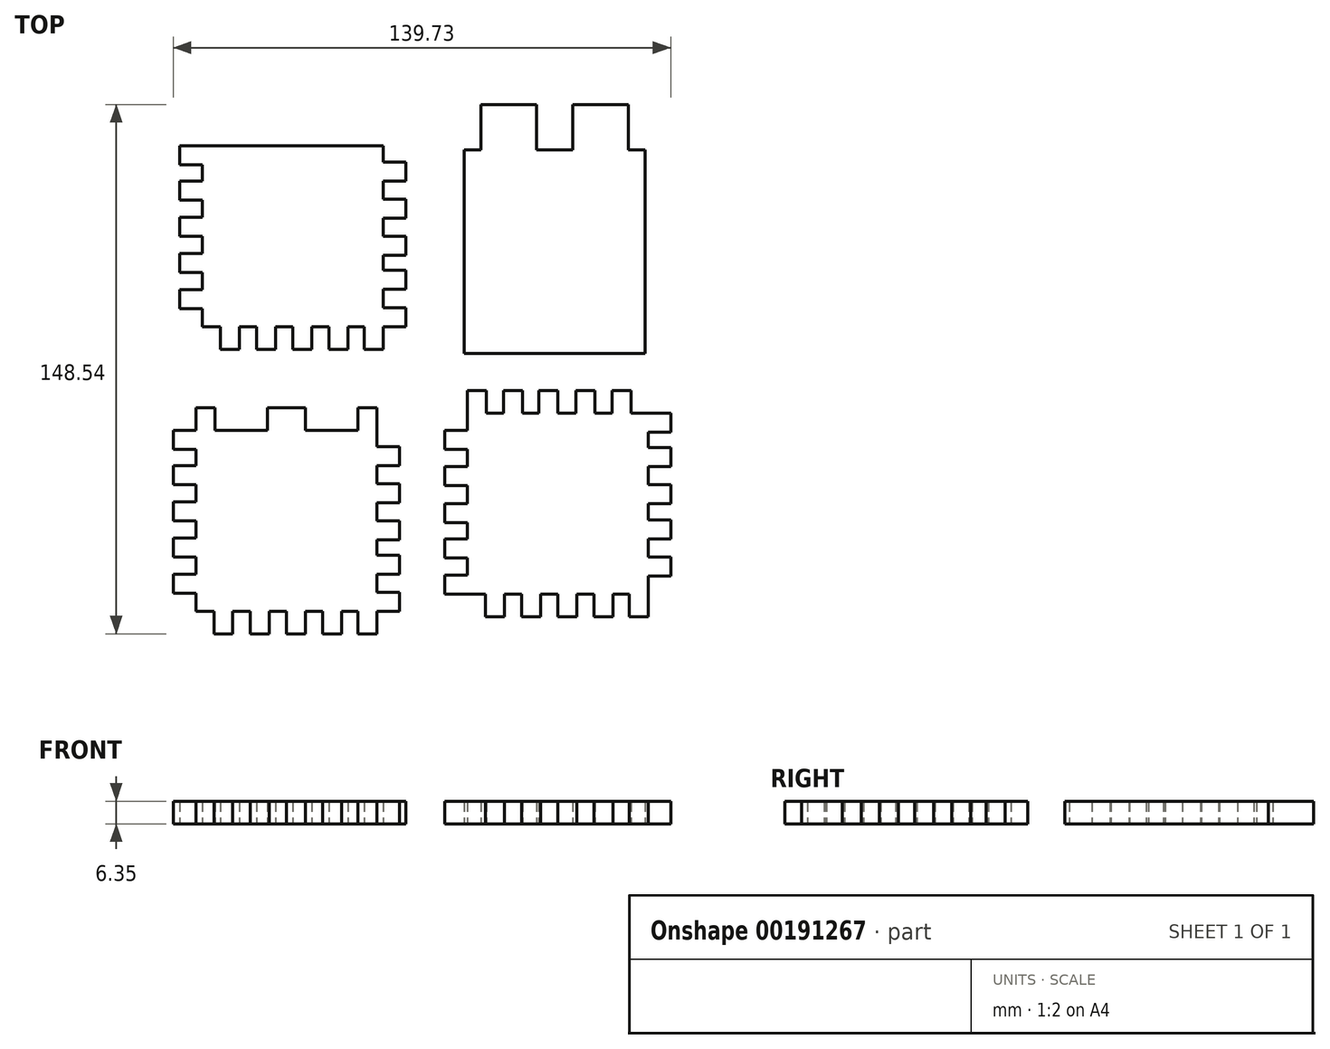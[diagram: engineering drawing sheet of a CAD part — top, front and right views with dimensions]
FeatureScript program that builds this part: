
annotation { "Feature Type Name" : "Feature", "Feature Type Description" : "" }
export const myFeature = defineFeature(function(context is Context, id is Id, definition is map)
    precondition{}
    {
        {
            var Q0;
            Q0=qCreatedBy(makeId("Top.planeOp"),FACE);
            var sketch = newSketch(context, id + "F0", { "sketchPlane" : qUnion([Q0])});
            skLineSegment(sketch, "E0.bottom", {"start": v(-10.8, 18.02) * mm, "end": v(-61.6, 18.02) * mm});
            skLineSegment(sketch, "E0.top", {"start": v(-10.8, 68.82) * mm, "end": v(-61.6, 68.82) * mm});
            skLineSegment(sketch, "E0.left", {"start": v(-10.8, 18.02) * mm, "end": v(-10.8, 68.82) * mm});
            skLineSegment(sketch, "E0.right", {"start": v(-61.6, 18.02) * mm, "end": v(-61.6, 68.82) * mm});
            skLineSegment(sketch, "E1.bottom", {"start": v(-61.6, 68.82) * mm, "end": v(-67.96, 68.82) * mm});
            skLineSegment(sketch, "E1.top", {"start": v(-61.6, 63.48) * mm, "end": v(-67.96, 63.48) * mm});
            skLineSegment(sketch, "E1.left", {"start": v(-61.6, 68.82) * mm, "end": v(-61.6, 63.48) * mm});
            skLineSegment(sketch, "E1.right", {"start": v(-67.96, 68.82) * mm, "end": v(-67.96, 63.48) * mm});
            skLineSegment(sketch, "E2.top", {"start": v(-61.6, 58.91) * mm, "end": v(-67.96, 58.91) * mm});
            skLineSegment(sketch, "E2.left", {"start": v(-61.6, 63.48) * mm, "end": v(-61.6, 58.91) * mm});
            skLineSegment(sketch, "E3.top", {"start": v(-61.6, 53.58) * mm, "end": v(-67.96, 53.58) * mm});
            skLineSegment(sketch, "E3.left", {"start": v(-61.6, 58.91) * mm, "end": v(-61.6, 53.58) * mm});
            skLineSegment(sketch, "E3.right", {"start": v(-67.96, 58.91) * mm, "end": v(-67.96, 53.58) * mm});
            skLineSegment(sketch, "E4.left", {"start": v(-61.6, 53.58) * mm, "end": v(-61.6, 48.75) * mm});
            skLineSegment(sketch, "E5.bottom", {"start": v(-61.6, 48.75) * mm, "end": v(-67.96, 48.75) * mm});
            skLineSegment(sketch, "E5.left", {"start": v(-61.6, 48.75) * mm, "end": v(-61.6, 53.58) * mm});
            skLineSegment(sketch, "E6.left", {"start": v(-61.6, 48.75) * mm, "end": v(-61.6, 38.6) * mm});
            skLineSegment(sketch, "E7.bottom", {"start": v(-67.96, 48.75) * mm, "end": v(-61.6, 48.75) * mm});
            skLineSegment(sketch, "E7.top", {"start": v(-67.96, 43.42) * mm, "end": v(-61.6, 43.42) * mm});
            skLineSegment(sketch, "E7.left", {"start": v(-67.96, 48.75) * mm, "end": v(-67.96, 43.42) * mm});
            skLineSegment(sketch, "E7.right", {"start": v(-61.6, 48.75) * mm, "end": v(-61.6, 43.42) * mm});
            skLineSegment(sketch, "E8.top", {"start": v(-67.96, 38.6) * mm, "end": v(-61.6, 38.6) * mm});
            skLineSegment(sketch, "E8.right", {"start": v(-61.6, 43.42) * mm, "end": v(-61.6, 38.6) * mm});
            skLineSegment(sketch, "E9.top", {"start": v(-67.96, 33.26) * mm, "end": v(-61.6, 33.26) * mm});
            skLineSegment(sketch, "E9.left", {"start": v(-67.96, 38.6) * mm, "end": v(-67.96, 33.26) * mm});
            skLineSegment(sketch, "E9.right", {"start": v(-61.6, 38.6) * mm, "end": v(-61.6, 33.26) * mm});
            skLineSegment(sketch, "E10.top", {"start": v(-67.96, 28.43) * mm, "end": v(-61.6, 28.43) * mm});
            skLineSegment(sketch, "E10.right", {"start": v(-61.6, 33.26) * mm, "end": v(-61.6, 28.43) * mm});
            skLineSegment(sketch, "E11.top", {"start": v(-67.96, 23.1) * mm, "end": v(-61.6, 23.1) * mm});
            skLineSegment(sketch, "E11.left", {"start": v(-67.96, 28.43) * mm, "end": v(-67.96, 23.1) * mm});
            skLineSegment(sketch, "E11.right", {"start": v(-61.6, 28.43) * mm, "end": v(-61.6, 23.1) * mm});
            skLineSegment(sketch, "E12.right", {"start": v(-61.6, 23.1) * mm, "end": v(-61.6, 18.02) * mm});
            skLineSegment(sketch, "E13.top", {"start": v(-10.8, 64.24) * mm, "end": v(-4.46, 64.24) * mm});
            skLineSegment(sketch, "E13.left", {"start": v(-10.8, 68.82) * mm, "end": v(-10.8, 64.24) * mm});
            skLineSegment(sketch, "E14.bottom", {"start": v(-4.46, 64.24) * mm, "end": v(-10.8, 64.24) * mm});
            skLineSegment(sketch, "E14.top", {"start": v(-4.46, 58.91) * mm, "end": v(-10.8, 58.91) * mm});
            skLineSegment(sketch, "E14.left", {"start": v(-4.46, 64.24) * mm, "end": v(-4.46, 58.91) * mm});
            skLineSegment(sketch, "E14.right", {"start": v(-10.8, 64.24) * mm, "end": v(-10.8, 58.91) * mm});
            skLineSegment(sketch, "E15.top", {"start": v(-4.46, 53.83) * mm, "end": v(-10.8, 53.83) * mm});
            skLineSegment(sketch, "E15.right", {"start": v(-10.8, 58.91) * mm, "end": v(-10.8, 53.83) * mm});
            skLineSegment(sketch, "E16.top", {"start": v(-4.46, 48.5) * mm, "end": v(-10.8, 48.5) * mm});
            skLineSegment(sketch, "E16.left", {"start": v(-4.46, 53.83) * mm, "end": v(-4.46, 48.5) * mm});
            skLineSegment(sketch, "E16.right", {"start": v(-10.8, 53.83) * mm, "end": v(-10.8, 48.5) * mm});
            skLineSegment(sketch, "E17.top", {"start": v(-4.46, 43.42) * mm, "end": v(-10.8, 43.42) * mm});
            skLineSegment(sketch, "E17.right", {"start": v(-10.8, 48.5) * mm, "end": v(-10.8, 43.42) * mm});
            skLineSegment(sketch, "E18.top", {"start": v(-4.46, 38.08) * mm, "end": v(-10.8, 38.08) * mm});
            skLineSegment(sketch, "E18.left", {"start": v(-4.46, 43.42) * mm, "end": v(-4.46, 38.08) * mm});
            skLineSegment(sketch, "E18.right", {"start": v(-10.8, 43.42) * mm, "end": v(-10.8, 38.08) * mm});
            skLineSegment(sketch, "E19.top", {"start": v(-4.46, 33.9) * mm, "end": v(-10.8, 33.9) * mm});
            skLineSegment(sketch, "E19.right", {"start": v(-10.8, 38.08) * mm, "end": v(-10.8, 33.9) * mm});
            skLineSegment(sketch, "E20.top", {"start": v(-4.46, 28.56) * mm, "end": v(-10.8, 28.56) * mm});
            skLineSegment(sketch, "E20.left", {"start": v(-4.46, 33.9) * mm, "end": v(-4.46, 28.56) * mm});
            skLineSegment(sketch, "E20.right", {"start": v(-10.8, 33.9) * mm, "end": v(-10.8, 28.56) * mm});
            skLineSegment(sketch, "E21.top", {"start": v(-4.46, 23.35) * mm, "end": v(-10.8, 23.35) * mm});
            skLineSegment(sketch, "E21.right", {"start": v(-10.8, 28.56) * mm, "end": v(-10.8, 23.35) * mm});
            skLineSegment(sketch, "E22.top", {"start": v(-4.46, 18.02) * mm, "end": v(-10.8, 18.02) * mm});
            skLineSegment(sketch, "E22.left", {"start": v(-4.46, 23.35) * mm, "end": v(-4.46, 18.02) * mm});
            skLineSegment(sketch, "E22.right", {"start": v(-10.8, 23.35) * mm, "end": v(-10.8, 18.02) * mm});
            skLineSegment(sketch, "E23.bottom", {"start": v(-10.8, 18.02) * mm, "end": v(-16.14, 18.02) * mm});
            skLineSegment(sketch, "E23.top", {"start": v(-10.8, 11.67) * mm, "end": v(-16.14, 11.67) * mm});
            skLineSegment(sketch, "E23.left", {"start": v(-10.8, 18.02) * mm, "end": v(-10.8, 11.67) * mm});
            skLineSegment(sketch, "E23.right", {"start": v(-16.14, 18.02) * mm, "end": v(-16.14, 11.67) * mm});
            skLineSegment(sketch, "E24.top", {"start": v(-16.14, 18.02) * mm, "end": v(-20.71, 18.02) * mm});
            skLineSegment(sketch, "E24.left", {"start": v(-16.14, 11.67) * mm, "end": v(-16.14, 18.02) * mm});
            skLineSegment(sketch, "E24.right", {"start": v(-20.71, 11.67) * mm, "end": v(-20.71, 18.02) * mm});
            skLineSegment(sketch, "E25.bottom", {"start": v(-20.71, 11.67) * mm, "end": v(-26.05, 11.67) * mm});
            skLineSegment(sketch, "E25.top", {"start": v(-20.71, 18.02) * mm, "end": v(-26.05, 18.02) * mm});
            skLineSegment(sketch, "E25.right", {"start": v(-26.05, 11.67) * mm, "end": v(-26.05, 18.02) * mm});
            skLineSegment(sketch, "E26.top", {"start": v(-26.05, 18.02) * mm, "end": v(-30.87, 18.02) * mm});
            skLineSegment(sketch, "E26.right", {"start": v(-30.87, 11.67) * mm, "end": v(-30.87, 18.02) * mm});
            skLineSegment(sketch, "E27.bottom", {"start": v(-30.87, 11.67) * mm, "end": v(-36.2, 11.67) * mm});
            skLineSegment(sketch, "E27.top", {"start": v(-30.87, 18.02) * mm, "end": v(-36.2, 18.02) * mm});
            skLineSegment(sketch, "E27.right", {"start": v(-36.2, 11.67) * mm, "end": v(-36.2, 18.02) * mm});
            skLineSegment(sketch, "E28.top", {"start": v(-36.2, 18.02) * mm, "end": v(-41.03, 18.02) * mm});
            skLineSegment(sketch, "E28.right", {"start": v(-41.03, 11.67) * mm, "end": v(-41.03, 18.02) * mm});
            skLineSegment(sketch, "E29.bottom", {"start": v(-41.03, 11.67) * mm, "end": v(-46.37, 11.67) * mm});
            skLineSegment(sketch, "E29.top", {"start": v(-41.03, 18.02) * mm, "end": v(-46.37, 18.02) * mm});
            skLineSegment(sketch, "E29.right", {"start": v(-46.37, 11.67) * mm, "end": v(-46.37, 18.02) * mm});
            skLineSegment(sketch, "E30.top", {"start": v(-46.37, 18.02) * mm, "end": v(-51.2, 18.02) * mm});
            skLineSegment(sketch, "E30.right", {"start": v(-51.2, 11.67) * mm, "end": v(-51.2, 18.02) * mm});
            skLineSegment(sketch, "E31.bottom", {"start": v(-51.2, 11.67) * mm, "end": v(-56.53, 11.67) * mm});
            skLineSegment(sketch, "E31.top", {"start": v(-51.2, 18.02) * mm, "end": v(-56.53, 18.02) * mm});
            skLineSegment(sketch, "E31.right", {"start": v(-56.53, 11.67) * mm, "end": v(-56.53, 18.02) * mm});
            skLineSegment(sketch, "E32.top", {"start": v(-56.53, 18.02) * mm, "end": v(-61.6, 18.02) * mm});
            skSolve(sketch);
        }
        {
            var Q0;
            Q0 = qSketchRegion(id + "F0", true);
            extrude(context, id + "F1", {"entities" : qUnion([Q0]), "depth" : 6.35 * mm});
        }
        {
            var Q0;
            Q0=qCreatedBy(makeId("Top.planeOp"),FACE);
            var sketch = newSketch(context, id + "F2", { "sketchPlane" : qUnion([Q0])});
            skLineSegment(sketch, "E33.bottom", {"start": v(12.75, -6.35) * mm, "end": v(63.55, -6.35) * mm});
            skLineSegment(sketch, "E33.top", {"start": v(12.75, -57.15) * mm, "end": v(63.55, -57.15) * mm});
            skLineSegment(sketch, "E33.left", {"start": v(12.75, -6.35) * mm, "end": v(12.75, -57.15) * mm});
            skLineSegment(sketch, "E33.right", {"start": v(63.55, -6.35) * mm, "end": v(63.55, -57.15) * mm});
            skLineSegment(sketch, "E34.bottom", {"start": v(12.75, -6.35) * mm, "end": v(18.09, -6.35) * mm});
            skLineSegment(sketch, "E34.top", {"start": v(12.75, 0) * mm, "end": v(18.09, 0) * mm});
            skLineSegment(sketch, "E34.left", {"start": v(12.75, -6.35) * mm, "end": v(12.75, 0) * mm});
            skLineSegment(sketch, "E34.right", {"start": v(18.09, -6.35) * mm, "end": v(18.09, 0) * mm});
            skLineSegment(sketch, "E35.top", {"start": v(18.09, -6.35) * mm, "end": v(22.91, -6.35) * mm});
            skLineSegment(sketch, "E35.left", {"start": v(18.09, 0) * mm, "end": v(18.09, -6.35) * mm});
            skLineSegment(sketch, "E35.right", {"start": v(22.91, 0) * mm, "end": v(22.91, -6.35) * mm});
            skLineSegment(sketch, "E36.bottom", {"start": v(22.91, 0) * mm, "end": v(28.25, 0) * mm});
            skLineSegment(sketch, "E36.top", {"start": v(22.91, -6.35) * mm, "end": v(28.25, -6.35) * mm});
            skLineSegment(sketch, "E36.right", {"start": v(28.25, 0) * mm, "end": v(28.25, -6.35) * mm});
            skLineSegment(sketch, "E37.top", {"start": v(28.25, -6.35) * mm, "end": v(32.82, -6.35) * mm});
            skLineSegment(sketch, "E37.right", {"start": v(32.82, 0) * mm, "end": v(32.82, -6.35) * mm});
            skLineSegment(sketch, "E38.bottom", {"start": v(32.82, 0) * mm, "end": v(38.15, 0) * mm});
            skLineSegment(sketch, "E38.top", {"start": v(32.82, -6.35) * mm, "end": v(38.15, -6.35) * mm});
            skLineSegment(sketch, "E38.right", {"start": v(38.15, 0) * mm, "end": v(38.15, -6.35) * mm});
            skLineSegment(sketch, "E39.top", {"start": v(38.15, -6.35) * mm, "end": v(43.23, -6.35) * mm});
            skLineSegment(sketch, "E39.right", {"start": v(43.23, 0) * mm, "end": v(43.23, -6.35) * mm});
            skLineSegment(sketch, "E40.bottom", {"start": v(43.23, 0) * mm, "end": v(48.57, 0) * mm});
            skLineSegment(sketch, "E40.top", {"start": v(43.23, -6.35) * mm, "end": v(48.57, -6.35) * mm});
            skLineSegment(sketch, "E40.right", {"start": v(48.57, 0) * mm, "end": v(48.57, -6.35) * mm});
            skLineSegment(sketch, "E41.top", {"start": v(48.57, -6.35) * mm, "end": v(53.4, -6.35) * mm});
            skLineSegment(sketch, "E41.right", {"start": v(53.4, 0) * mm, "end": v(53.4, -6.35) * mm});
            skLineSegment(sketch, "E42.bottom", {"start": v(53.4, -6.35) * mm, "end": v(58.73, -6.35) * mm});
            skLineSegment(sketch, "E42.top", {"start": v(53.4, 0) * mm, "end": v(58.73, 0) * mm});
            skLineSegment(sketch, "E42.left", {"start": v(53.4, -6.35) * mm, "end": v(53.4, 0) * mm});
            skLineSegment(sketch, "E42.right", {"start": v(58.73, -6.35) * mm, "end": v(58.73, 0) * mm});
            skLineSegment(sketch, "E43.bottom", {"start": v(63.55, -6.35) * mm, "end": v(58.73, -6.35) * mm});
            skLineSegment(sketch, "E44.top", {"start": v(12.75, -11.18) * mm, "end": v(6.4, -11.18) * mm});
            skLineSegment(sketch, "E44.left", {"start": v(12.75, -6.35) * mm, "end": v(12.75, -11.18) * mm});
            skLineSegment(sketch, "E45.bottom", {"start": v(6.4, -11.18) * mm, "end": v(12.75, -11.18) * mm});
            skLineSegment(sketch, "E45.top", {"start": v(6.4, -16.5) * mm, "end": v(12.75, -16.5) * mm});
            skLineSegment(sketch, "E45.left", {"start": v(6.4, -11.18) * mm, "end": v(6.4, -16.5) * mm});
            skLineSegment(sketch, "E45.right", {"start": v(12.75, -11.18) * mm, "end": v(12.75, -16.5) * mm});
            skLineSegment(sketch, "E46.top", {"start": v(6.4, -21.34) * mm, "end": v(12.75, -21.34) * mm});
            skLineSegment(sketch, "E46.right", {"start": v(12.75, -16.5) * mm, "end": v(12.75, -21.34) * mm});
            skLineSegment(sketch, "E47.top", {"start": v(6.4, -26.67) * mm, "end": v(12.75, -26.67) * mm});
            skLineSegment(sketch, "E47.left", {"start": v(6.4, -21.34) * mm, "end": v(6.4, -26.67) * mm});
            skLineSegment(sketch, "E47.right", {"start": v(12.75, -21.34) * mm, "end": v(12.75, -26.67) * mm});
            skLineSegment(sketch, "E48.top", {"start": v(6.4, -31.75) * mm, "end": v(12.75, -31.75) * mm});
            skLineSegment(sketch, "E48.right", {"start": v(12.75, -26.67) * mm, "end": v(12.75, -31.75) * mm});
            skLineSegment(sketch, "E49.top", {"start": v(6.4, -37.08) * mm, "end": v(12.75, -37.08) * mm});
            skLineSegment(sketch, "E49.left", {"start": v(6.4, -31.75) * mm, "end": v(6.4, -37.08) * mm});
            skLineSegment(sketch, "E50.top", {"start": v(6.4, -41.66) * mm, "end": v(12.75, -41.66) * mm});
            skLineSegment(sketch, "E50.right", {"start": v(12.75, -37.08) * mm, "end": v(12.75, -41.66) * mm});
            skLineSegment(sketch, "E51.top", {"start": v(6.4, -47) * mm, "end": v(12.75, -47) * mm});
            skLineSegment(sketch, "E51.left", {"start": v(6.4, -41.66) * mm, "end": v(6.4, -47) * mm});
            skLineSegment(sketch, "E51.right", {"start": v(12.75, -41.66) * mm, "end": v(12.75, -47) * mm});
            skLineSegment(sketch, "E52.top", {"start": v(6.4, -51.82) * mm, "end": v(12.75, -51.82) * mm});
            skLineSegment(sketch, "E52.right", {"start": v(12.75, -47) * mm, "end": v(12.75, -51.82) * mm});
            skLineSegment(sketch, "E53.top", {"start": v(6.4, -57.15) * mm, "end": v(12.75, -57.15) * mm});
            skLineSegment(sketch, "E53.left", {"start": v(6.4, -51.82) * mm, "end": v(6.4, -57.15) * mm});
            skLineSegment(sketch, "E53.right", {"start": v(12.75, -51.82) * mm, "end": v(12.75, -57.15) * mm});
            skLineSegment(sketch, "E54.bottom", {"start": v(12.75, -57.15) * mm, "end": v(17.83, -57.15) * mm});
            skLineSegment(sketch, "E54.right", {"start": v(17.83, -57.15) * mm, "end": v(17.83, -63.5) * mm});
            skLineSegment(sketch, "E55.bottom", {"start": v(17.83, -63.5) * mm, "end": v(23.17, -63.5) * mm});
            skLineSegment(sketch, "E55.top", {"start": v(17.83, -57.15) * mm, "end": v(23.17, -57.15) * mm});
            skLineSegment(sketch, "E55.left", {"start": v(17.83, -63.5) * mm, "end": v(17.83, -57.15) * mm});
            skLineSegment(sketch, "E55.right", {"start": v(23.17, -63.5) * mm, "end": v(23.17, -57.15) * mm});
            skLineSegment(sketch, "E56.top", {"start": v(23.17, -57.15) * mm, "end": v(28, -57.15) * mm});
            skLineSegment(sketch, "E56.right", {"start": v(28, -63.5) * mm, "end": v(28, -57.15) * mm});
            skLineSegment(sketch, "E57.bottom", {"start": v(28, -63.5) * mm, "end": v(33.33, -63.5) * mm});
            skLineSegment(sketch, "E57.top", {"start": v(28, -57.15) * mm, "end": v(33.33, -57.15) * mm});
            skLineSegment(sketch, "E57.right", {"start": v(33.33, -63.5) * mm, "end": v(33.33, -57.15) * mm});
            skLineSegment(sketch, "E58.top", {"start": v(33.33, -57.15) * mm, "end": v(38.15, -57.15) * mm});
            skLineSegment(sketch, "E58.right", {"start": v(38.15, -63.5) * mm, "end": v(38.15, -57.15) * mm});
            skLineSegment(sketch, "E59.bottom", {"start": v(38.15, -63.5) * mm, "end": v(43.49, -63.5) * mm});
            skLineSegment(sketch, "E59.top", {"start": v(38.15, -57.15) * mm, "end": v(43.49, -57.15) * mm});
            skLineSegment(sketch, "E59.right", {"start": v(43.49, -63.5) * mm, "end": v(43.49, -57.15) * mm});
            skLineSegment(sketch, "E60.top", {"start": v(43.49, -57.15) * mm, "end": v(48.31, -57.15) * mm});
            skLineSegment(sketch, "E60.right", {"start": v(48.31, -63.5) * mm, "end": v(48.31, -57.15) * mm});
            skLineSegment(sketch, "E61.bottom", {"start": v(48.31, -63.5) * mm, "end": v(53.65, -63.5) * mm});
            skLineSegment(sketch, "E61.top", {"start": v(48.31, -57.15) * mm, "end": v(53.65, -57.15) * mm});
            skLineSegment(sketch, "E61.right", {"start": v(53.65, -63.5) * mm, "end": v(53.65, -57.15) * mm});
            skLineSegment(sketch, "E62.top", {"start": v(53.65, -57.15) * mm, "end": v(58.22, -57.15) * mm});
            skLineSegment(sketch, "E62.right", {"start": v(58.22, -63.5) * mm, "end": v(58.22, -57.15) * mm});
            skLineSegment(sketch, "E63.bottom", {"start": v(58.22, -63.5) * mm, "end": v(63.55, -63.5) * mm});
            skLineSegment(sketch, "E63.top", {"start": v(58.22, -57.15) * mm, "end": v(63.55, -57.15) * mm});
            skLineSegment(sketch, "E63.right", {"start": v(63.55, -63.5) * mm, "end": v(63.55, -57.15) * mm});
            skLineSegment(sketch, "E64.bottom", {"start": v(63.55, -6.35) * mm, "end": v(69.9, -6.35) * mm});
            skLineSegment(sketch, "E64.top", {"start": v(63.55, -11.68) * mm, "end": v(69.9, -11.68) * mm});
            skLineSegment(sketch, "E64.left", {"start": v(63.55, -6.35) * mm, "end": v(63.55, -11.68) * mm});
            skLineSegment(sketch, "E64.right", {"start": v(69.9, -6.35) * mm, "end": v(69.9, -11.68) * mm});
            skLineSegment(sketch, "E65.bottom", {"start": v(69.9, -11.68) * mm, "end": v(63.55, -11.68) * mm});
            skLineSegment(sketch, "E65.top", {"start": v(69.9, -16) * mm, "end": v(63.55, -16) * mm});
            skLineSegment(sketch, "E65.right", {"start": v(63.55, -11.68) * mm, "end": v(63.55, -16) * mm});
            skLineSegment(sketch, "E66.top", {"start": v(69.9, -21.34) * mm, "end": v(63.55, -21.34) * mm});
            skLineSegment(sketch, "E66.left", {"start": v(69.9, -16) * mm, "end": v(69.9, -21.34) * mm});
            skLineSegment(sketch, "E66.right", {"start": v(63.55, -16) * mm, "end": v(63.55, -21.34) * mm});
            skLineSegment(sketch, "E67.top", {"start": v(69.9, -26.42) * mm, "end": v(63.55, -26.42) * mm});
            skLineSegment(sketch, "E67.right", {"start": v(63.55, -21.34) * mm, "end": v(63.55, -26.42) * mm});
            skLineSegment(sketch, "E68.top", {"start": v(69.9, -31.75) * mm, "end": v(63.55, -31.75) * mm});
            skLineSegment(sketch, "E68.left", {"start": v(69.9, -26.42) * mm, "end": v(69.9, -31.75) * mm});
            skLineSegment(sketch, "E68.right", {"start": v(63.55, -26.42) * mm, "end": v(63.55, -31.75) * mm});
            skLineSegment(sketch, "E69.top", {"start": v(69.9, -36.32) * mm, "end": v(63.55, -36.32) * mm});
            skLineSegment(sketch, "E69.right", {"start": v(63.55, -31.75) * mm, "end": v(63.55, -36.32) * mm});
            skLineSegment(sketch, "E70.top", {"start": v(69.9, -41.66) * mm, "end": v(63.55, -41.66) * mm});
            skLineSegment(sketch, "E70.left", {"start": v(69.9, -36.32) * mm, "end": v(69.9, -41.66) * mm});
            skLineSegment(sketch, "E70.right", {"start": v(63.55, -36.32) * mm, "end": v(63.55, -41.66) * mm});
            skLineSegment(sketch, "E71.top", {"start": v(69.9, -46.74) * mm, "end": v(63.55, -46.74) * mm});
            skLineSegment(sketch, "E71.right", {"start": v(63.55, -41.66) * mm, "end": v(63.55, -46.74) * mm});
            skLineSegment(sketch, "E72.top", {"start": v(69.9, -52.07) * mm, "end": v(63.55, -52.07) * mm});
            skLineSegment(sketch, "E72.left", {"start": v(69.9, -46.74) * mm, "end": v(69.9, -52.07) * mm});
            skLineSegment(sketch, "E72.right", {"start": v(63.55, -46.74) * mm, "end": v(63.55, -52.07) * mm});
            skSolve(sketch);
        }
        {
            var Q0;
            Q0 = qSketchRegion(id + "F2", true);
            extrude(context, id + "F3", {"entities" : qUnion([Q0]), "depth" : 6.35 * mm});
        }
        {
            var Q0;
            Q0=qCreatedBy(makeId("Top.planeOp"),FACE);
            var sketch = newSketch(context, id + "F4", { "sketchPlane" : qUnion([Q0])});
            skLineSegment(sketch, "E73.bottom", {"start": v(-12.68, -61.89) * mm, "end": v(-63.48, -61.89) * mm});
            skLineSegment(sketch, "E73.top", {"start": v(-12.68, -11.09) * mm, "end": v(-63.48, -11.09) * mm});
            skLineSegment(sketch, "E73.left", {"start": v(-12.68, -61.89) * mm, "end": v(-12.68, -11.09) * mm});
            skLineSegment(sketch, "E73.right", {"start": v(-63.48, -61.89) * mm, "end": v(-63.48, -11.09) * mm});
            skLineSegment(sketch, "E74.bottom", {"start": v(-63.48, -11.09) * mm, "end": v(-69.83, -11.09) * mm});
            skLineSegment(sketch, "E74.top", {"start": v(-63.48, -16.42) * mm, "end": v(-69.83, -16.42) * mm});
            skLineSegment(sketch, "E74.left", {"start": v(-63.48, -11.09) * mm, "end": v(-63.48, -16.42) * mm});
            skLineSegment(sketch, "E74.right", {"start": v(-69.83, -11.09) * mm, "end": v(-69.83, -16.42) * mm});
            skLineSegment(sketch, "E75.top", {"start": v(-63.48, -21) * mm, "end": v(-69.83, -21) * mm});
            skLineSegment(sketch, "E75.left", {"start": v(-63.48, -16.42) * mm, "end": v(-63.48, -21) * mm});
            skLineSegment(sketch, "E76.top", {"start": v(-63.48, -26.33) * mm, "end": v(-69.83, -26.33) * mm});
            skLineSegment(sketch, "E76.left", {"start": v(-63.48, -21) * mm, "end": v(-63.48, -26.33) * mm});
            skLineSegment(sketch, "E76.right", {"start": v(-69.83, -21) * mm, "end": v(-69.83, -26.33) * mm});
            skLineSegment(sketch, "E77.left", {"start": v(-63.48, -26.33) * mm, "end": v(-63.48, -31.15) * mm});
            skLineSegment(sketch, "E78.bottom", {"start": v(-63.48, -31.15) * mm, "end": v(-69.83, -31.15) * mm});
            skLineSegment(sketch, "E78.left", {"start": v(-63.48, -31.15) * mm, "end": v(-63.48, -26.33) * mm});
            skLineSegment(sketch, "E79.left", {"start": v(-63.48, -31.15) * mm, "end": v(-63.48, -41.31) * mm});
            skLineSegment(sketch, "E80.bottom", {"start": v(-69.83, -31.15) * mm, "end": v(-63.48, -31.15) * mm});
            skLineSegment(sketch, "E80.top", {"start": v(-69.83, -36.49) * mm, "end": v(-63.48, -36.49) * mm});
            skLineSegment(sketch, "E80.left", {"start": v(-69.83, -31.15) * mm, "end": v(-69.83, -36.49) * mm});
            skLineSegment(sketch, "E80.right", {"start": v(-63.48, -31.15) * mm, "end": v(-63.48, -36.49) * mm});
            skLineSegment(sketch, "E81.top", {"start": v(-69.83, -41.31) * mm, "end": v(-63.48, -41.31) * mm});
            skLineSegment(sketch, "E81.right", {"start": v(-63.48, -36.49) * mm, "end": v(-63.48, -41.31) * mm});
            skLineSegment(sketch, "E82.top", {"start": v(-69.83, -46.65) * mm, "end": v(-63.48, -46.65) * mm});
            skLineSegment(sketch, "E82.left", {"start": v(-69.83, -41.31) * mm, "end": v(-69.83, -46.65) * mm});
            skLineSegment(sketch, "E82.right", {"start": v(-63.48, -41.31) * mm, "end": v(-63.48, -46.65) * mm});
            skLineSegment(sketch, "E83.top", {"start": v(-69.83, -51.47) * mm, "end": v(-63.48, -51.47) * mm});
            skLineSegment(sketch, "E83.right", {"start": v(-63.48, -46.65) * mm, "end": v(-63.48, -51.47) * mm});
            skLineSegment(sketch, "E84.top", {"start": v(-69.83, -56.8) * mm, "end": v(-63.48, -56.8) * mm});
            skLineSegment(sketch, "E84.left", {"start": v(-69.83, -51.47) * mm, "end": v(-69.83, -56.8) * mm});
            skLineSegment(sketch, "E84.right", {"start": v(-63.48, -51.47) * mm, "end": v(-63.48, -56.8) * mm});
            skLineSegment(sketch, "E85.right", {"start": v(-63.48, -56.8) * mm, "end": v(-63.48, -61.89) * mm});
            skLineSegment(sketch, "E86.top", {"start": v(-12.68, -15.66) * mm, "end": v(-6.33, -15.66) * mm});
            skLineSegment(sketch, "E86.left", {"start": v(-12.68, -11.09) * mm, "end": v(-12.68, -15.66) * mm});
            skLineSegment(sketch, "E87.bottom", {"start": v(-6.33, -15.66) * mm, "end": v(-12.68, -15.66) * mm});
            skLineSegment(sketch, "E87.top", {"start": v(-6.33, -21) * mm, "end": v(-12.68, -21) * mm});
            skLineSegment(sketch, "E87.left", {"start": v(-6.33, -15.66) * mm, "end": v(-6.33, -21) * mm});
            skLineSegment(sketch, "E87.right", {"start": v(-12.68, -15.66) * mm, "end": v(-12.68, -21) * mm});
            skLineSegment(sketch, "E88.top", {"start": v(-6.33, -26.07) * mm, "end": v(-12.68, -26.07) * mm});
            skLineSegment(sketch, "E88.right", {"start": v(-12.68, -21) * mm, "end": v(-12.68, -26.07) * mm});
            skLineSegment(sketch, "E89.top", {"start": v(-6.33, -31.4) * mm, "end": v(-12.68, -31.4) * mm});
            skLineSegment(sketch, "E89.left", {"start": v(-6.33, -26.07) * mm, "end": v(-6.33, -31.4) * mm});
            skLineSegment(sketch, "E89.right", {"start": v(-12.68, -26.07) * mm, "end": v(-12.68, -31.4) * mm});
            skLineSegment(sketch, "E90.top", {"start": v(-6.33, -36.49) * mm, "end": v(-12.68, -36.49) * mm});
            skLineSegment(sketch, "E90.right", {"start": v(-12.68, -31.4) * mm, "end": v(-12.68, -36.49) * mm});
            skLineSegment(sketch, "E91.top", {"start": v(-6.33, -41.82) * mm, "end": v(-12.68, -41.82) * mm});
            skLineSegment(sketch, "E91.left", {"start": v(-6.33, -36.49) * mm, "end": v(-6.33, -41.82) * mm});
            skLineSegment(sketch, "E91.right", {"start": v(-12.68, -36.49) * mm, "end": v(-12.68, -41.82) * mm});
            skLineSegment(sketch, "E92.top", {"start": v(-6.33, -46.14) * mm, "end": v(-12.68, -46.14) * mm});
            skLineSegment(sketch, "E92.right", {"start": v(-12.68, -41.82) * mm, "end": v(-12.68, -46.14) * mm});
            skLineSegment(sketch, "E93.top", {"start": v(-6.33, -51.47) * mm, "end": v(-12.68, -51.47) * mm});
            skLineSegment(sketch, "E93.left", {"start": v(-6.33, -46.14) * mm, "end": v(-6.33, -51.47) * mm});
            skLineSegment(sketch, "E93.right", {"start": v(-12.68, -46.14) * mm, "end": v(-12.68, -51.47) * mm});
            skLineSegment(sketch, "E94.top", {"start": v(-6.33, -56.55) * mm, "end": v(-12.68, -56.55) * mm});
            skLineSegment(sketch, "E94.right", {"start": v(-12.68, -51.47) * mm, "end": v(-12.68, -56.55) * mm});
            skLineSegment(sketch, "E95.top", {"start": v(-6.33, -61.89) * mm, "end": v(-12.68, -61.89) * mm});
            skLineSegment(sketch, "E95.left", {"start": v(-6.33, -56.55) * mm, "end": v(-6.33, -61.89) * mm});
            skLineSegment(sketch, "E95.right", {"start": v(-12.68, -56.55) * mm, "end": v(-12.68, -61.89) * mm});
            skLineSegment(sketch, "E96.bottom", {"start": v(-12.68, -61.89) * mm, "end": v(-18.02, -61.89) * mm});
            skLineSegment(sketch, "E96.top", {"start": v(-12.68, -68.24) * mm, "end": v(-18.02, -68.24) * mm});
            skLineSegment(sketch, "E96.left", {"start": v(-12.68, -61.89) * mm, "end": v(-12.68, -68.24) * mm});
            skLineSegment(sketch, "E96.right", {"start": v(-18.02, -61.89) * mm, "end": v(-18.02, -68.24) * mm});
            skLineSegment(sketch, "E97.top", {"start": v(-18.02, -61.89) * mm, "end": v(-22.59, -61.89) * mm});
            skLineSegment(sketch, "E97.left", {"start": v(-18.02, -68.24) * mm, "end": v(-18.02, -61.89) * mm});
            skLineSegment(sketch, "E97.right", {"start": v(-22.59, -68.24) * mm, "end": v(-22.59, -61.89) * mm});
            skLineSegment(sketch, "E98.bottom", {"start": v(-22.59, -68.24) * mm, "end": v(-27.92, -68.24) * mm});
            skLineSegment(sketch, "E98.top", {"start": v(-22.59, -61.89) * mm, "end": v(-27.92, -61.89) * mm});
            skLineSegment(sketch, "E98.right", {"start": v(-27.92, -68.24) * mm, "end": v(-27.92, -61.89) * mm});
            skLineSegment(sketch, "E99.top", {"start": v(-27.92, -61.89) * mm, "end": v(-32.75, -61.89) * mm});
            skLineSegment(sketch, "E99.right", {"start": v(-32.75, -68.24) * mm, "end": v(-32.75, -61.89) * mm});
            skLineSegment(sketch, "E100.bottom", {"start": v(-32.75, -68.24) * mm, "end": v(-38.08, -68.24) * mm});
            skLineSegment(sketch, "E100.top", {"start": v(-32.75, -61.89) * mm, "end": v(-38.08, -61.89) * mm});
            skLineSegment(sketch, "E100.right", {"start": v(-38.08, -68.24) * mm, "end": v(-38.08, -61.89) * mm});
            skLineSegment(sketch, "E101.top", {"start": v(-38.08, -61.89) * mm, "end": v(-42.9, -61.89) * mm});
            skLineSegment(sketch, "E101.right", {"start": v(-42.9, -68.24) * mm, "end": v(-42.9, -61.89) * mm});
            skLineSegment(sketch, "E102.bottom", {"start": v(-42.9, -68.24) * mm, "end": v(-48.24, -68.24) * mm});
            skLineSegment(sketch, "E102.top", {"start": v(-42.9, -61.89) * mm, "end": v(-48.24, -61.89) * mm});
            skLineSegment(sketch, "E102.right", {"start": v(-48.24, -68.24) * mm, "end": v(-48.24, -61.89) * mm});
            skLineSegment(sketch, "E103.top", {"start": v(-48.24, -61.89) * mm, "end": v(-53.07, -61.89) * mm});
            skLineSegment(sketch, "E103.right", {"start": v(-53.07, -68.24) * mm, "end": v(-53.07, -61.89) * mm});
            skLineSegment(sketch, "E104.bottom", {"start": v(-53.07, -68.24) * mm, "end": v(-58.4, -68.24) * mm});
            skLineSegment(sketch, "E104.top", {"start": v(-53.07, -61.89) * mm, "end": v(-58.4, -61.89) * mm});
            skLineSegment(sketch, "E104.right", {"start": v(-58.4, -68.24) * mm, "end": v(-58.4, -61.89) * mm});
            skLineSegment(sketch, "E105.top", {"start": v(-58.4, -61.89) * mm, "end": v(-63.48, -61.89) * mm});
            skLineSegment(sketch, "E106.bottom", {"start": v(-63.48, -11.09) * mm, "end": v(-56.54, -11.09) * mm});
            skLineSegment(sketch, "E107.bottom", {"start": v(-12.68, -11.09) * mm, "end": v(-23.13, -11.09) * mm});
            skLineSegment(sketch, "E108.bottom", {"start": v(-63.48, -11.09) * mm, "end": v(-58.15, -11.09) * mm});
            skLineSegment(sketch, "E108.top", {"start": v(-63.48, -4.74) * mm, "end": v(-58.15, -4.74) * mm});
            skLineSegment(sketch, "E108.left", {"start": v(-63.48, -11.09) * mm, "end": v(-63.48, -4.74) * mm});
            skLineSegment(sketch, "E108.right", {"start": v(-58.15, -11.09) * mm, "end": v(-58.15, -4.74) * mm});
            skLineSegment(sketch, "E109.bottom", {"start": v(-12.68, -11.09) * mm, "end": v(-18.02, -11.09) * mm});
            skLineSegment(sketch, "E109.top", {"start": v(-12.68, -4.74) * mm, "end": v(-18.02, -4.74) * mm});
            skLineSegment(sketch, "E109.left", {"start": v(-12.68, -11.09) * mm, "end": v(-12.68, -4.74) * mm});
            skLineSegment(sketch, "E109.right", {"start": v(-18.02, -11.09) * mm, "end": v(-18.02, -4.74) * mm});
            skLineSegment(sketch, "E110.bottom", {"start": v(-38.08, -11.09) * mm, "end": v(-43.42, -11.09) * mm});
            skLineSegment(sketch, "E110.top", {"start": v(-38.08, -4.74) * mm, "end": v(-43.42, -4.74) * mm});
            skLineSegment(sketch, "E110.left", {"start": v(-38.08, -11.09) * mm, "end": v(-38.08, -4.74) * mm});
            skLineSegment(sketch, "E110.right", {"start": v(-43.42, -11.09) * mm, "end": v(-43.42, -4.74) * mm});
            skLineSegment(sketch, "E111.bottom", {"start": v(-38.08, -11.09) * mm, "end": v(-32.75, -11.09) * mm});
            skLineSegment(sketch, "E111.top", {"start": v(-38.08, -4.74) * mm, "end": v(-32.75, -4.74) * mm});
            skLineSegment(sketch, "E111.right", {"start": v(-32.75, -11.09) * mm, "end": v(-32.75, -4.74) * mm});
            skSolve(sketch);
        }
        {
            var Q0;
            Q0 = qSketchRegion(id + "F4", true);
            extrude(context, id + "F5", {"entities" : qUnion([Q0]), "depth" : 6.35 * mm});
        }
        {
            var Q0;
            Q0=qCreatedBy(makeId("Top.planeOp"),FACE);
            var sketch = newSketch(context, id + "F6", { "sketchPlane" : qUnion([Q0])});
            skLineSegment(sketch, "E112.bottom", {"start": v(11.92, 67.6) * mm, "end": v(62.72, 67.6) * mm});
            skLineSegment(sketch, "E112.top", {"start": v(11.92, 10.45) * mm, "end": v(62.72, 10.45) * mm});
            skLineSegment(sketch, "E112.left", {"start": v(11.92, 67.6) * mm, "end": v(11.92, 10.45) * mm});
            skLineSegment(sketch, "E112.right", {"start": v(62.72, 67.6) * mm, "end": v(62.72, 10.45) * mm});
            skLineSegment(sketch, "E113.bottom", {"start": v(11.92, 67.6) * mm, "end": v(16.62, 67.6) * mm});
            skLineSegment(sketch, "E113.right", {"start": v(16.62, 67.6) * mm, "end": v(16.62, 80.3) * mm});
            skLineSegment(sketch, "E114.bottom", {"start": v(62.72, 67.6) * mm, "end": v(58.03, 67.6) * mm});
            skLineSegment(sketch, "E114.right", {"start": v(58.03, 67.6) * mm, "end": v(58.03, 80.3) * mm});
            skLineSegment(sketch, "E115.bottom", {"start": v(37.32, 67.6) * mm, "end": v(42.4, 67.6) * mm});
            skLineSegment(sketch, "E115.right", {"start": v(42.4, 67.6) * mm, "end": v(42.4, 80.3) * mm});
            skLineSegment(sketch, "E116.bottom", {"start": v(37.32, 67.6) * mm, "end": v(32.24, 67.6) * mm});
            skLineSegment(sketch, "E116.right", {"start": v(32.24, 67.6) * mm, "end": v(32.24, 80.3) * mm});
            skLineSegment(sketch, "E117.bottom", {"start": v(16.62, 80.3) * mm, "end": v(32.24, 80.3) * mm});
            skLineSegment(sketch, "E117.top", {"start": v(16.62, 67.6) * mm, "end": v(32.24, 67.6) * mm});
            skLineSegment(sketch, "E117.left", {"start": v(16.62, 80.3) * mm, "end": v(16.62, 67.6) * mm});
            skLineSegment(sketch, "E117.right", {"start": v(32.24, 80.3) * mm, "end": v(32.24, 67.6) * mm});
            skLineSegment(sketch, "E118.bottom", {"start": v(42.4, 67.6) * mm, "end": v(58.03, 67.6) * mm});
            skLineSegment(sketch, "E118.top", {"start": v(42.4, 80.3) * mm, "end": v(58.03, 80.3) * mm});
            skSolve(sketch);
        }
        {
            var Q0;
            Q0 = qSketchRegion(id + "F6", true);
            extrude(context, id + "F7", {"entities" : qUnion([Q0]), "depth" : 6.35 * mm});
        }
    });
